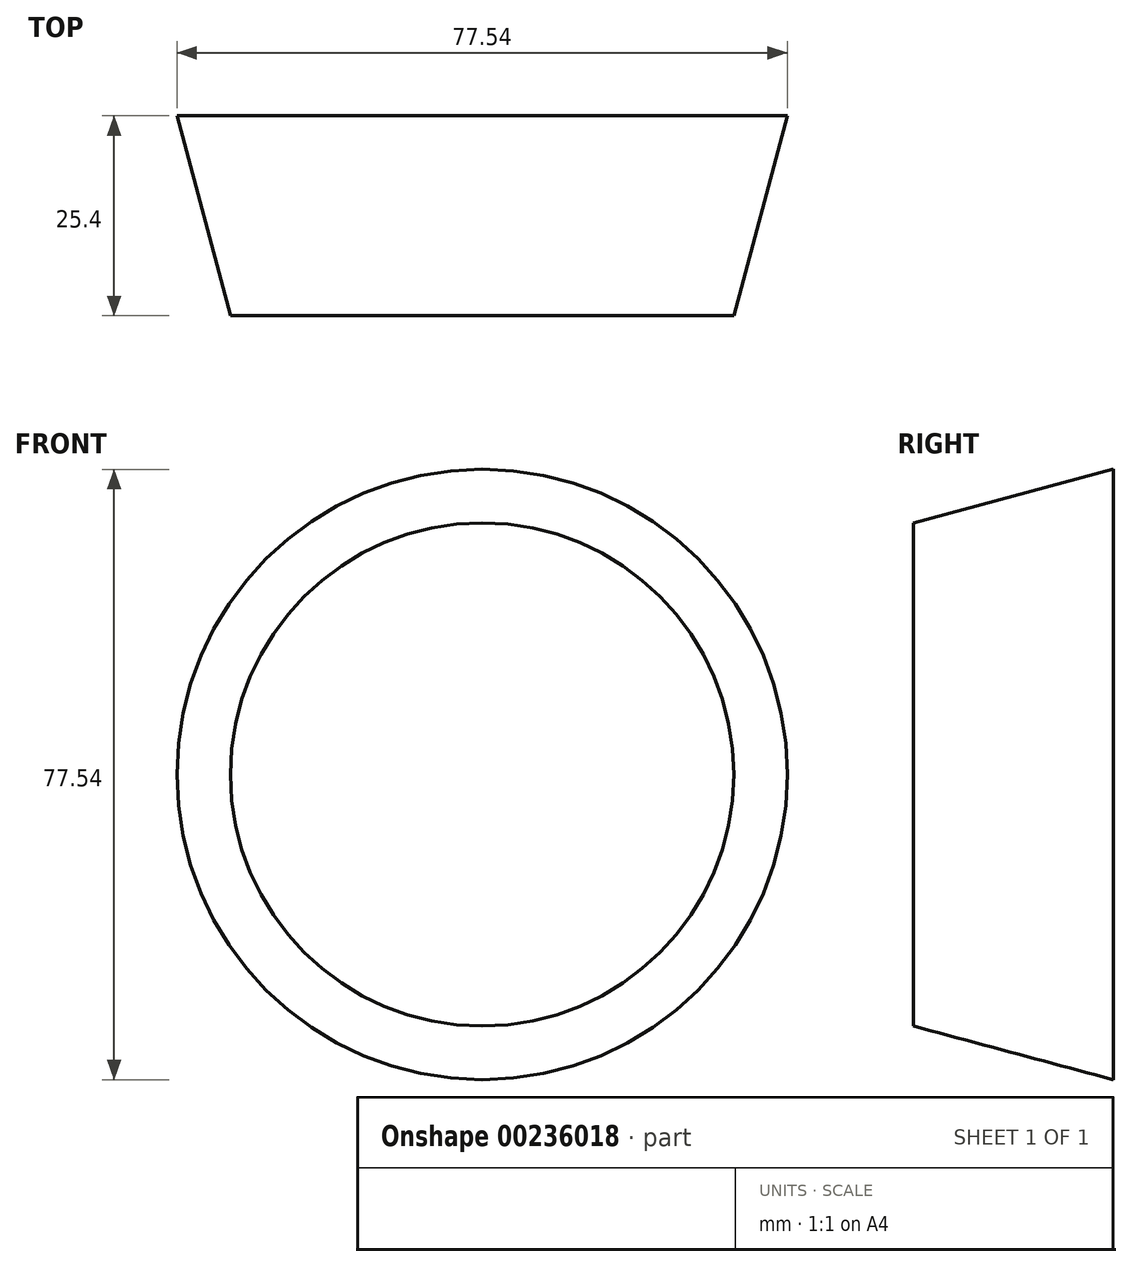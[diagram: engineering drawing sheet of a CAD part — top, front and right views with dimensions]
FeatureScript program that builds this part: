
annotation { "Feature Type Name" : "Feature", "Feature Type Description" : "" }
export const myFeature = defineFeature(function(context is Context, id is Id, definition is map)
    precondition{}
    {
        {
            var Q0;
            Q0=qCreatedBy(makeId("Front.planeOp"),FACE);
            var sketch = newSketch(context, id + "F0", { "sketchPlane" : qUnion([Q0])});
            skCircle(sketch, "E0", {"center": v(0, 0) * mm, "radius": 31.97 * mm});
            skSolve(sketch);
        }
        {
            var Q0;
            Q0 = qSketchRegion(id + "F0", true);
            extrude(context, id + "F1", {"entities" : qUnion([Q0]), "oppositeDirection" : true, "depth" : 25.4 * mm, "hasDraft" : true, "draftAngle" : 15 * degree});
        }
    });
